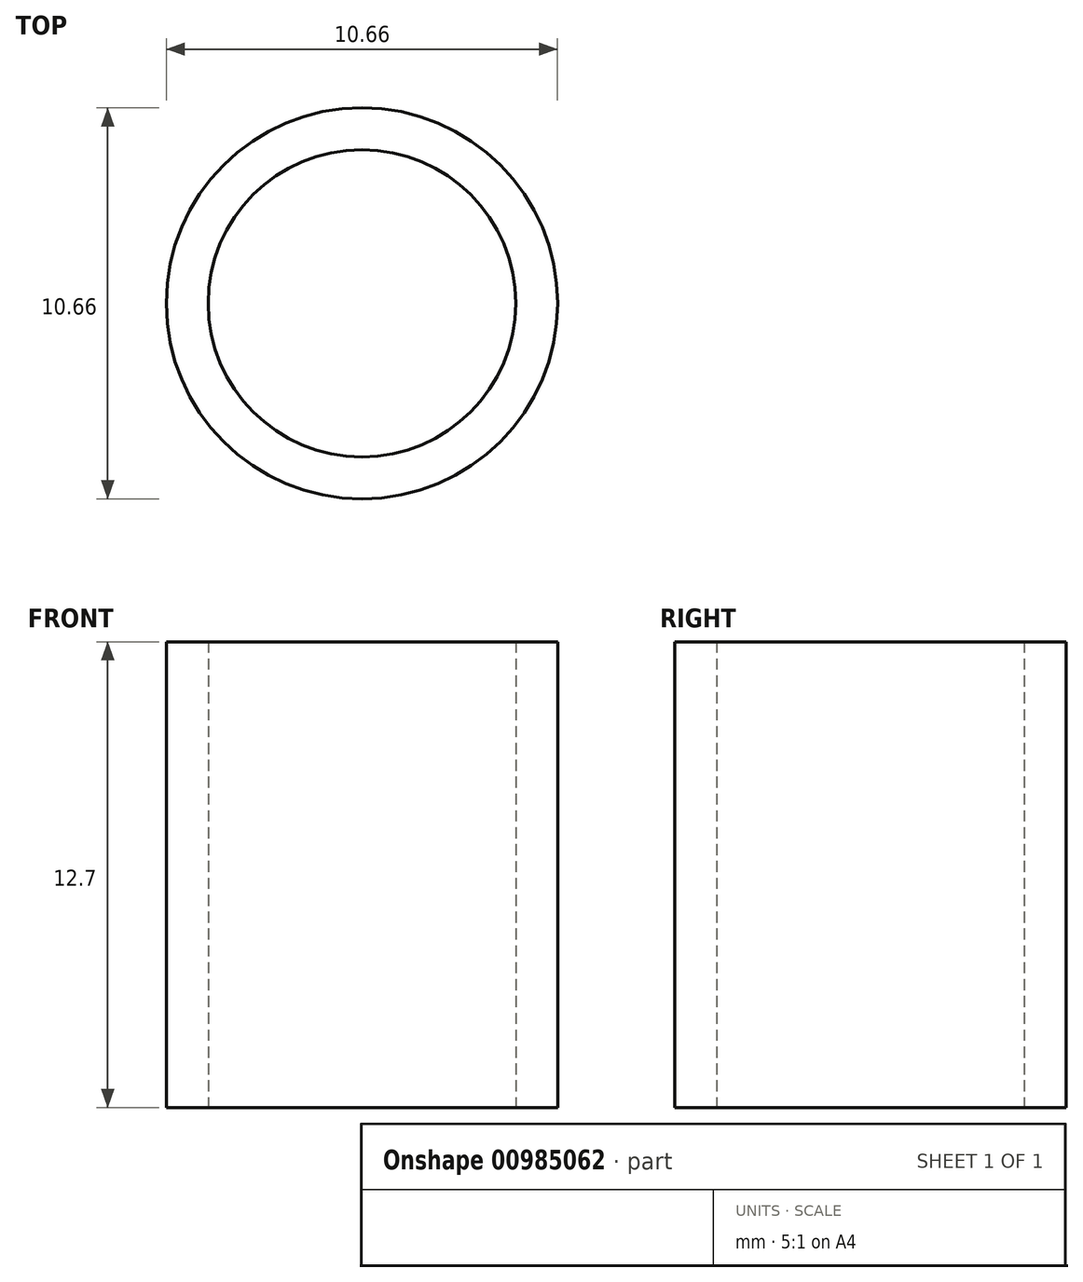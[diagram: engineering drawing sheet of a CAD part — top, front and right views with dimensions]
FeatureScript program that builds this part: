
annotation { "Feature Type Name" : "Feature", "Feature Type Description" : "" }
export const myFeature = defineFeature(function(context is Context, id is Id, definition is map)
    precondition{}
    {
        {
            var Q0;
            Q0=qCreatedBy(makeId("Top.planeOp"),FACE);
            var sketch = newSketch(context, id + "F0", { "sketchPlane" : qUnion([Q0])});
            skCircle(sketch, "E0", {"center": v(0, 0) * mm, "radius": 4.2 * mm});
            skCircle(sketch, "E1", {"center": v(0, 0) * mm, "radius": 5.33 * mm});
            skSolve(sketch);
        }
        {
            var Q0;
            Q0=makeQuery(id+"F0.imprint","IMPRINT",FACE,{"disambiguationData":[TD([[makeQuery(id+"F0.imprint","IMPRINT",EDGE,{"derivedFrom":sQuery(id+"F0.wireOp",EDGE,"E0")}),-1.0]])]});
            extrude(context, id + "F1", {"entities" : qUnion([Q0]), "depth" : 12.7 * mm, "offsetDistance" : 25.4 * mm});
        }
    });
